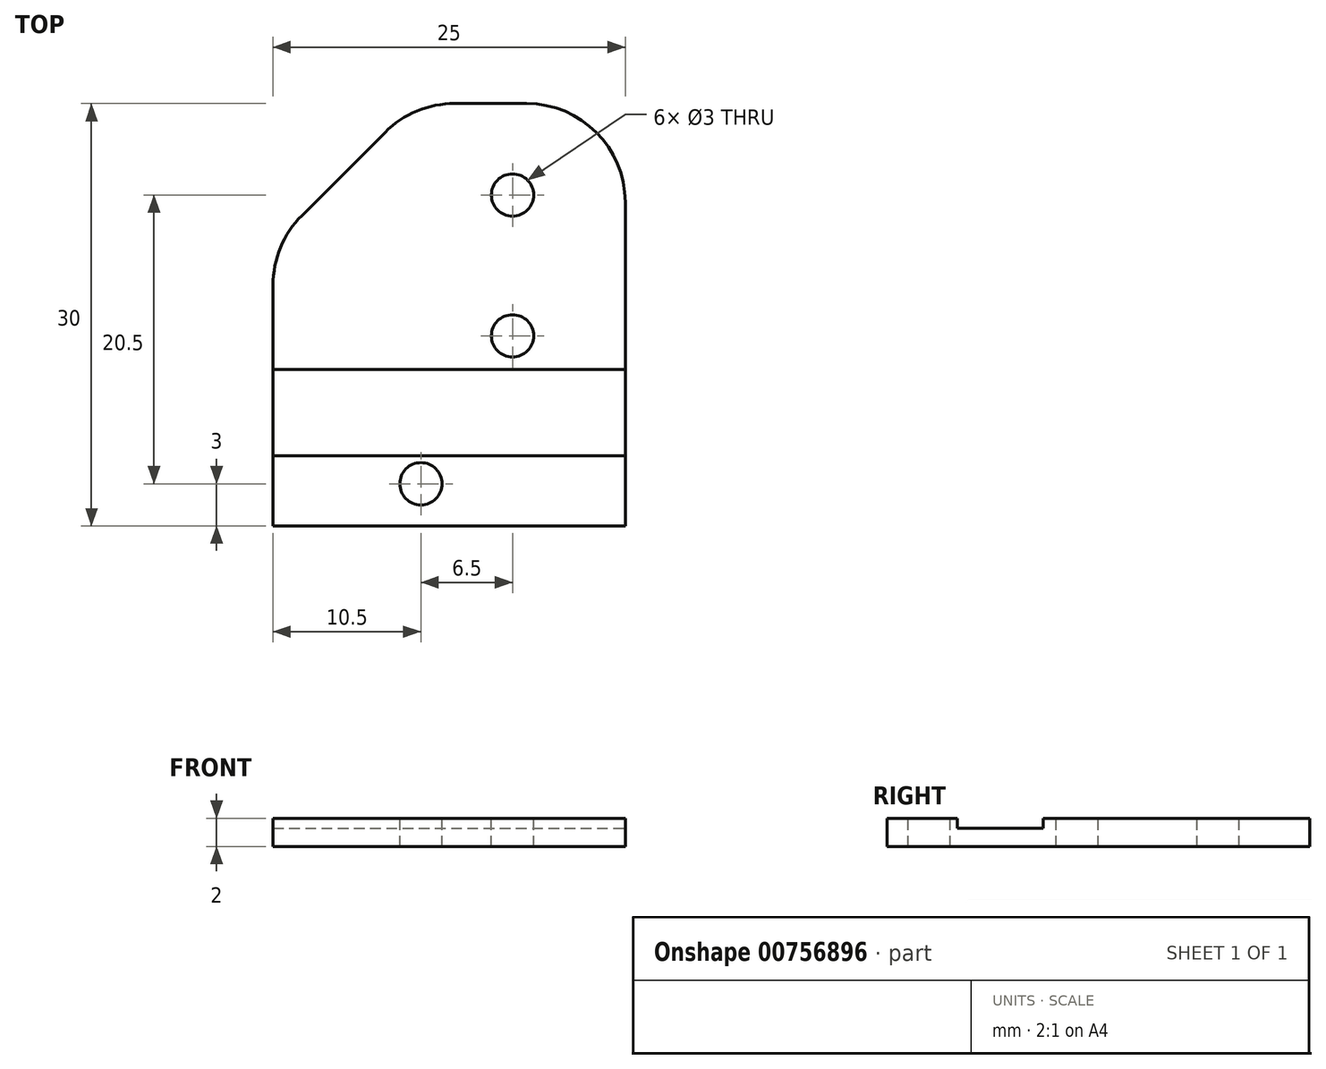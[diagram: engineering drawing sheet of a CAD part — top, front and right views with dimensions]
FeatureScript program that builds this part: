
annotation { "Feature Type Name" : "Feature", "Feature Type Description" : "" }
export const myFeature = defineFeature(function(context is Context, id is Id, definition is map)
    precondition{}
    {
        {
            var Q0;
            Q0=qCreatedBy(makeId("Top.planeOp"),FACE);
            var sketch = newSketch(context, id + "F0", { "sketchPlane" : qUnion([Q0])});
            skLineSegment(sketch, "E0.bottom", {"start": v(12.5, -15) * mm, "end": v(-12.5, -15) * mm});
            skLineSegment(sketch, "E0.top", {"start": v(12.5, 15) * mm, "end": v(-12.5, 15) * mm});
            skLineSegment(sketch, "E0.left", {"start": v(12.5, -15) * mm, "end": v(12.5, 15) * mm});
            skLineSegment(sketch, "E0.right", {"start": v(-12.5, -15) * mm, "end": v(-12.5, 15) * mm});
            skPoint(sketch, "E0.middle", {"position": v(0, 0) * mm});
            skSolve(sketch);
        }
        {
            var Q0;
            Q0=makeQuery(id+"F0.imprint","IMPRINT",FACE,{"disambiguationData":[TD([[makeQuery(id+"F0.imprint","IMPRINT",EDGE,{"derivedFrom":sQuery(id+"F0.wireOp",EDGE,"E0.bottom")}),-1.0]])]});
            extrude(context, id + "F1", {"entities" : qUnion([Q0]), "depth" : 2 * mm, "offsetDistance" : 25 * mm});
        }
        {
            var Q0;
            Q0=makeQuery(id+"F1.opExtrude","CAP_FACE",FACE,{"disambiguationData":[OSD([sQuery(id+"F0.wireOp",EDGE,"E0.bottom"),sQuery(id+"F0.wireOp",EDGE,"E0.top"),sQuery(id+"F0.wireOp",EDGE,"E0.left"),sQuery(id+"F0.wireOp",EDGE,"E0.right")])],"isStart":false});
            var sketch = newSketch(context, id + "F2", { "sketchPlane" : qUnion([Q0])});
            skCircle(sketch, "E1", {"center": v(-2, -12) * mm, "radius": 1.5 * mm});
            skPoint(sketch, "E1.centerSnap0", {"position": v(0, -15) * mm});
            skCircle(sketch, "E2", {"center": v(4.5, -1.5) * mm, "radius": 1.5 * mm});
            skCircle(sketch, "E3", {"center": v(4.5, 8.5) * mm, "radius": 1.5 * mm});
            skSolve(sketch);
        }
        {
            var Q0;
            Q0=qSketchRegion(id+"F2",true);
            extrude(context, id + "F3", {"entities" : qUnion([Q0]), "operationType" : NewBodyOperationType.REMOVE, "endBound" : BoundingType.THROUGH_ALL, "oppositeDirection" : true, "depth" : 25 * mm, "offsetDistance" : 25 * mm});
        }
        {
            var Q0;
            Q0=makeQuery(id+"F1.opExtrude","CAP_FACE",FACE,{"disambiguationData":[OSD([sQuery(id+"F0.wireOp",EDGE,"E0.bottom"),sQuery(id+"F0.wireOp",EDGE,"E0.top"),sQuery(id+"F0.wireOp",EDGE,"E0.left"),sQuery(id+"F0.wireOp",EDGE,"E0.right")])],"isStart":false});
            var sketch = newSketch(context, id + "F4", { "sketchPlane" : qUnion([Q0])});
            skLineSegment(sketch, "E4.bottom", {"start": v(-12.5, -3.9) * mm, "end": v(12.5, -3.9) * mm});
            skLineSegment(sketch, "E4.top", {"start": v(-12.5, -10) * mm, "end": v(12.5, -10) * mm});
            skLineSegment(sketch, "E4.left", {"start": v(-12.5, -3.9) * mm, "end": v(-12.5, -10) * mm});
            skLineSegment(sketch, "E4.right", {"start": v(12.5, -3.9) * mm, "end": v(12.5, -10) * mm});
            skPoint(sketch, "E4.middle", {"position": v(0, -6.95) * mm});
            skSolve(sketch);
        }
        {
            var Q0;
            Q0 = qSketchRegion(id + "F4", true);
            extrude(context, id + "F5", {"entities" : qUnion([Q0]), "operationType" : NewBodyOperationType.REMOVE, "oppositeDirection" : true, "depth" : 0.7 * mm, "offsetDistance" : 25 * mm});
        }
        {
            var Q0;
            Q0=makeQuery(id+"F1.opExtrude","SWEPT_EDGE",EDGE,{"disambiguationData":[OSD([sQuery(id+"F0.wireOp",EDGE,"E0.top"),sQuery(id+"F0.wireOp",EDGE,"E0.right")])]});
            chamfer(context, id + "F6", {"entities" : qUnion([Q0]), "width" : 10 * mm, "tangentPropagation" : true});
        }
        {
            var Q0;
            {var subQ0=sQuery(id+"F0.wireOp",EDGE,"E0.right");Q0=makeQuery(id+"F6.opChamfer","BLEND_EDGE",EDGE,{"blendedFrom":[makeQuery(id+"F1.opExtrude","SWEPT_EDGE",EDGE,{"disambiguationData":[OSD([sQuery(id+"F0.wireOp",EDGE,"E0.top"),subQ0])]}),makeQuery(id+"F1.opExtrude","SWEPT_FACE",FACE,{"disambiguationData":[OSD([subQ0])]})],"blendedInto":[makeQuery(id+"F1.opExtrude","SWEPT_FACE",FACE,{"disambiguationData":[OSD([subQ0])]})]});}
            var Q1;
            {var subQ0=sQuery(id+"F0.wireOp",EDGE,"E0.top");Q1=makeQuery(id+"F6.opChamfer","BLEND_EDGE",EDGE,{"blendedFrom":[makeQuery(id+"F1.opExtrude","SWEPT_EDGE",EDGE,{"disambiguationData":[OSD([subQ0,sQuery(id+"F0.wireOp",EDGE,"E0.right")])]}),makeQuery(id+"F1.opExtrude","SWEPT_FACE",FACE,{"disambiguationData":[OSD([subQ0])]})],"blendedInto":[makeQuery(id+"F1.opExtrude","SWEPT_FACE",FACE,{"disambiguationData":[OSD([subQ0])]})]});}
            var Q2;
            Q2=makeQuery(id+"F1.opExtrude","SWEPT_EDGE",EDGE,{"disambiguationData":[OSD([sQuery(id+"F0.wireOp",EDGE,"E0.top"),sQuery(id+"F0.wireOp",EDGE,"E0.left")])]});
            fillet(context, id + "F7", {"entities" : qUnion([Q0, Q1, Q2]), "radius" : 7 * mm, "tangentPropagation" : true, "allowEdgeOverflow" : false});
        }
    });
